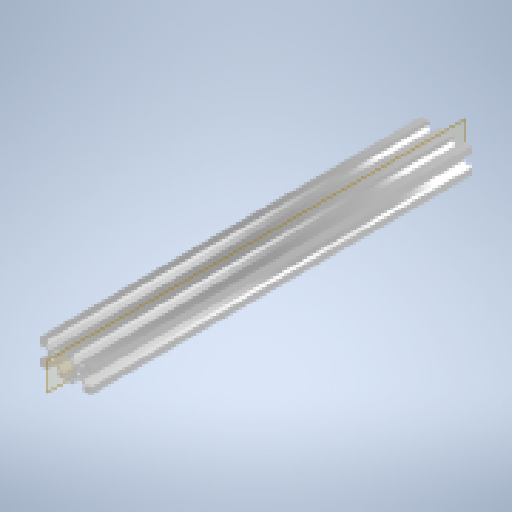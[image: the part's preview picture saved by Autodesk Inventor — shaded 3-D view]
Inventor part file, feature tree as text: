
AUTODESK INVENTOR PART (.ipt)
format: ipt  version: 2025.2 (Build 292293000, 293)  size: 385,536 bytes
history: native  units: in
note: dims shown in document units (in); Inventor stores cm internally (conversion verified against a paired STEP export)
features: plane x2, extrude x1, sketch x1, other x1
ambient origin geometry x8: Origin, YZ Plane, XZ Plane, XY Plane, X Axis, Y Axis, Z Axis, Center Point
bodies: Solid1 (feature_tree)
feature tree (5):
  extrude  "Extrusion1"  [1 undecoded]
  plane  "Work Plane1"
  plane  "Work Plane2"
  sketch  "Sketch1"  dims[d0=7.874in d1=0.0in]
  other  "Boss-Extrude1"
note: 1 required parameter value undecoded (feature->parameter linkage not recoverable at this tier; creation-order binding heuristic only, values carry confidence <= 0.55)
